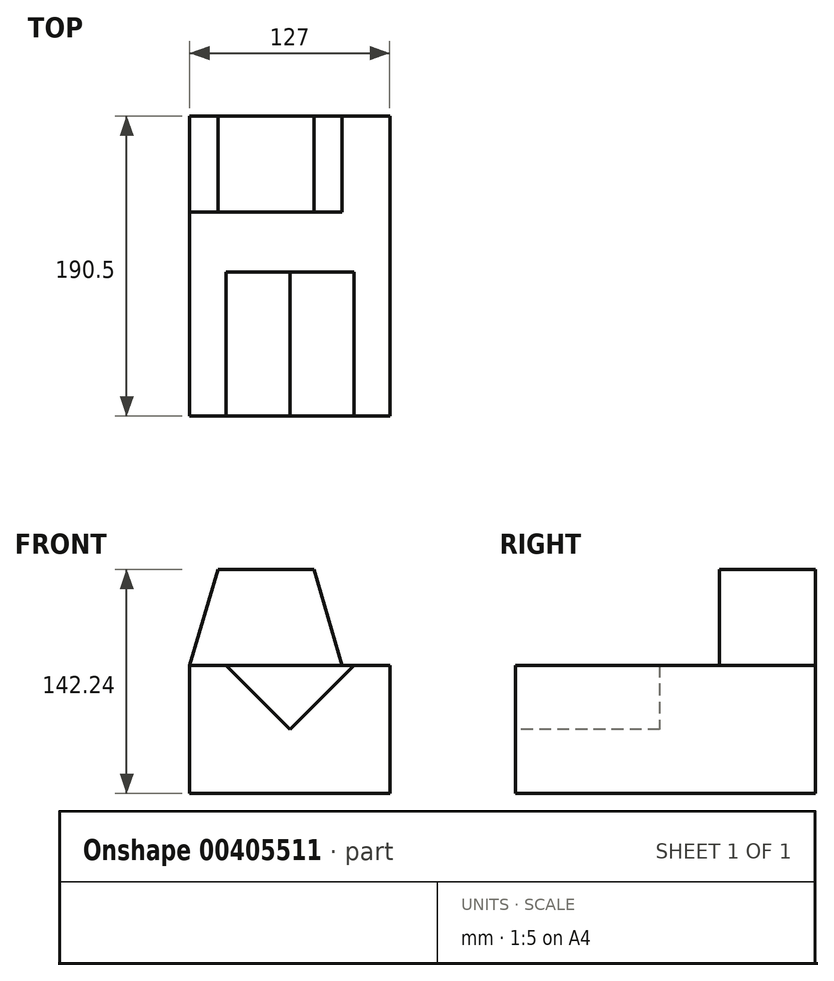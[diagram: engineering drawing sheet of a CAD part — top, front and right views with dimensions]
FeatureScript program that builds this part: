
annotation { "Feature Type Name" : "Feature", "Feature Type Description" : "" }
export const myFeature = defineFeature(function(context is Context, id is Id, definition is map)
    precondition{}
    {
        {
            var Q0;
            Q0=qCreatedBy(makeId("Top.planeOp"),FACE);
            var sketch = newSketch(context, id + "F0", { "sketchPlane" : qUnion([Q0])});
            skLineSegment(sketch, "E0.bottom", {"start": v(-63.72, 118.2) * mm, "end": v(63.28, 118.2) * mm});
            skLineSegment(sketch, "E0.top", {"start": v(-63.72, -72.3) * mm, "end": v(63.28, -72.3) * mm});
            skLineSegment(sketch, "E0.left", {"start": v(-63.72, 118.2) * mm, "end": v(-63.72, -72.3) * mm});
            skLineSegment(sketch, "E0.right", {"start": v(63.28, 118.2) * mm, "end": v(63.28, -72.3) * mm});
            skSolve(sketch);
        }
        {
            var Q0;
            Q0=makeQuery(id+"F0.imprint","IMPRINT",FACE,{"disambiguationData":[TD([[makeQuery(id+"F0.imprint","IMPRINT",EDGE,{"derivedFrom":sQuery(id+"F0.wireOp",EDGE,"E0.bottom")}),-1.0]])]});
            extrude(context, id + "F1", {"entities" : qUnion([Q0]), "depth" : 81.28 * mm});
        }
        {
            var Q0;
            Q0=makeQuery(id+"F1.opExtrude","SWEPT_FACE",FACE,{"disambiguationData":[OSD([sQuery(id+"F0.wireOp",EDGE,"E0.top")])]});
            var sketch = newSketch(context, id + "F2", { "sketchPlane" : qUnion([Q0])});
            skLineSegment(sketch, "E1", {"start": v(-40.86, 81.28) * mm, "end": v(-0.22, 40.64) * mm});
            skLineSegment(sketch, "E2", {"start": v(-0.22, 40.64) * mm, "end": v(40.42, 81.28) * mm});
            skSolve(sketch);
        }
        {
            var Q0;
            {var subQ0=sQuery(id+"F2.wireOp",EDGE,"E1");Q0=makeQuery(id+"F2.imprint","IMPRINT",FACE,{"disambiguationData":[TD([[makeQuery(id+"F2.imprint","IMPRINT",EDGE,{"derivedFrom":subQ0}),1.0]])]});}
            extrude(context, id + "F3", {"entities" : qUnion([Q0]), "operationType" : NewBodyOperationType.REMOVE, "oppositeDirection" : true, "depth" : 91.44 * mm});
        }
        {
            var Q0;
            Q0=makeQuery(id+"F1.opExtrude","CAP_FACE",FACE,{"disambiguationData":[OSD([sQuery(id+"F0.wireOp",EDGE,"E0.bottom"),sQuery(id+"F0.wireOp",EDGE,"E0.top"),sQuery(id+"F0.wireOp",EDGE,"E0.left"),sQuery(id+"F0.wireOp",EDGE,"E0.right")])],"isStart":false});
            var sketch = newSketch(context, id + "F4", { "sketchPlane" : qUnion([Q0])});
            skLineSegment(sketch, "E3.bottom", {"start": v(-63.72, 118.2) * mm, "end": v(32.8, 118.2) * mm});
            skLineSegment(sketch, "E3.top", {"start": v(-63.72, 57.25) * mm, "end": v(32.8, 57.25) * mm});
            skLineSegment(sketch, "E3.left", {"start": v(-63.72, 118.2) * mm, "end": v(-63.72, 57.25) * mm});
            skLineSegment(sketch, "E3.right", {"start": v(32.8, 118.2) * mm, "end": v(32.8, 57.25) * mm});
            skSolve(sketch);
        }
        {
            var Q0;
            Q0=makeQuery(id+"F4.imprint","IMPRINT",FACE,{"disambiguationData":[TD([[makeQuery(id+"F4.imprint","IMPRINT",EDGE,{"derivedFrom":sQuery(id+"F4.wireOp",EDGE,"E3.bottom")}),-1.0]])]});
            extrude(context, id + "F5", {"entities" : qUnion([Q0]), "operationType" : NewBodyOperationType.ADD, "depth" : 60.96 * mm});
        }
        {
            var Q0;
            Q0=makeQuery(id+"F5.opExtrude","SWEPT_FACE",FACE,{"disambiguationData":[OSD([sQuery(id+"F4.wireOp",EDGE,"E3.top")])]});
            var sketch = newSketch(context, id + "F6", { "sketchPlane" : qUnion([Q0])});
            skLineSegment(sketch, "E4", {"start": v(-63.72, 81.28) * mm, "end": v(-45.94, 142.24) * mm});
            skLineSegment(sketch, "E5", {"start": v(32.8, 81.28) * mm, "end": v(15.02, 142.24) * mm});
            skSolve(sketch);
        }
        {
            var Q0;
            {var subQ0=sQuery(id+"F6.wireOp",EDGE,"E4");Q0=makeQuery(id+"F6.imprint","IMPRINT",FACE,{"disambiguationData":[TD([[makeQuery(id+"F6.imprint","IMPRINT",EDGE,{"derivedFrom":subQ0}),1.0]])]});}
            var Q1;
            {var subQ0=sQuery(id+"F6.wireOp",EDGE,"E5");Q1=makeQuery(id+"F6.imprint","IMPRINT",FACE,{"disambiguationData":[TD([[makeQuery(id+"F6.imprint","IMPRINT",EDGE,{"derivedFrom":subQ0}),-1.0]])]});}
            extrude(context, id + "F7", {"entities" : qUnion([Q0, Q1]), "operationType" : NewBodyOperationType.REMOVE, "oppositeDirection" : true, "depth" : 60.96 * mm});
        }
    });
